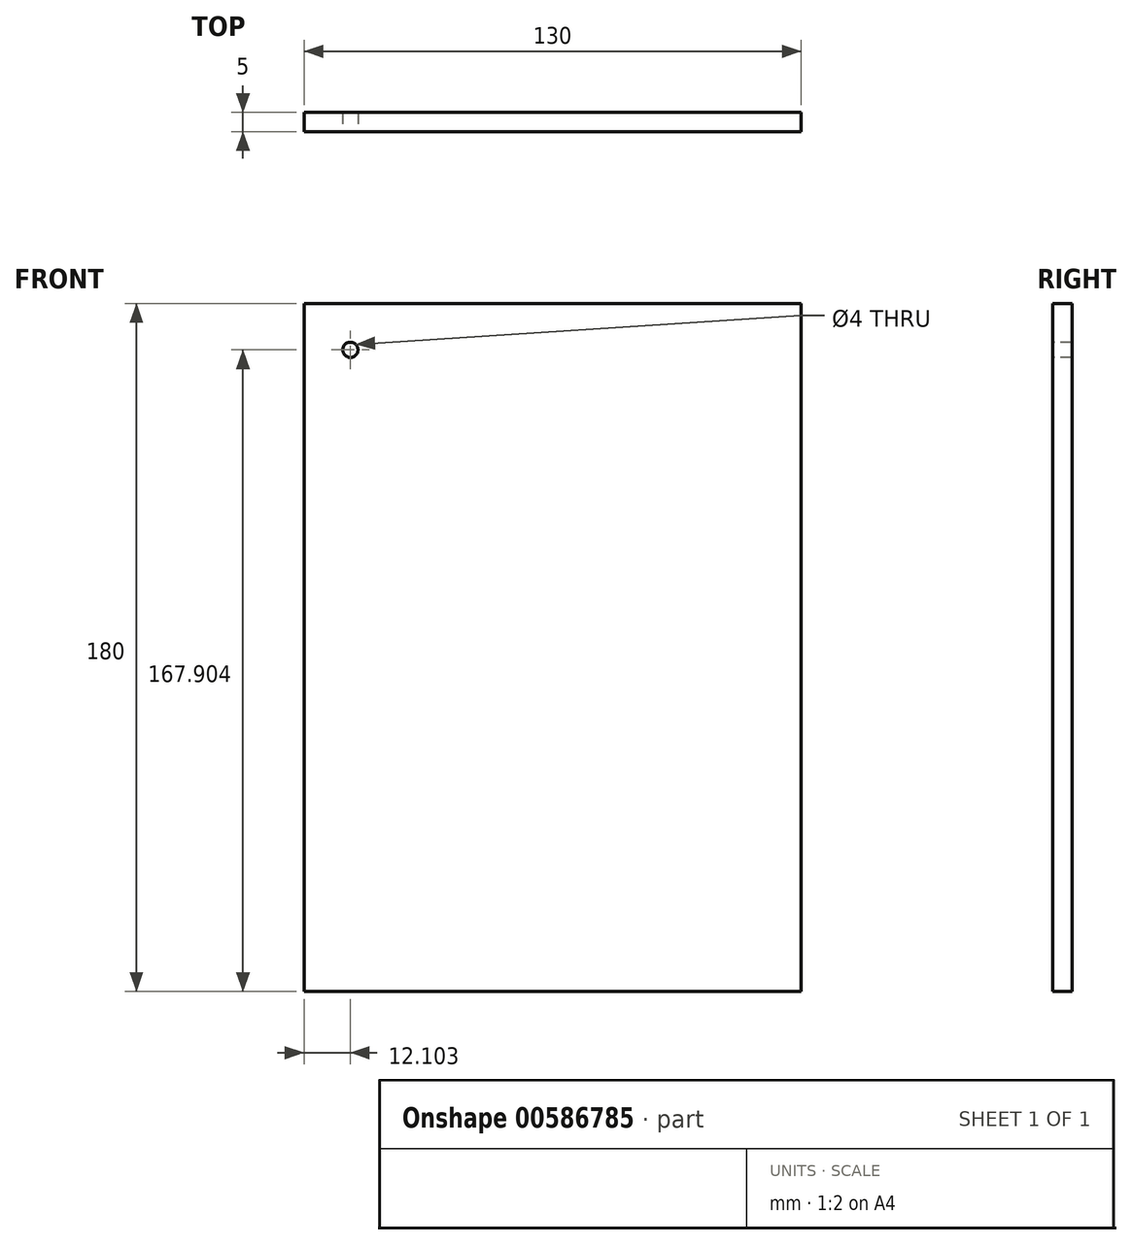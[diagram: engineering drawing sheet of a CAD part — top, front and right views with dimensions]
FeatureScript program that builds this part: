
annotation { "Feature Type Name" : "Feature", "Feature Type Description" : "" }
export const myFeature = defineFeature(function(context is Context, id is Id, definition is map)
    precondition{}
    {
        {
            var Q0;
            Q0=qCreatedBy(makeId("Front.planeOp"),FACE);
            var sketch = newSketch(context, id + "F0", { "sketchPlane" : qUnion([Q0])});
            skLineSegment(sketch, "E0.bottom", {"start": v(-69.83, 88.3) * mm, "end": v(60.17, 88.3) * mm});
            skLineSegment(sketch, "E0.top", {"start": v(-69.83, -91.7) * mm, "end": v(60.17, -91.7) * mm});
            skLineSegment(sketch, "E0.left", {"start": v(-69.83, 88.3) * mm, "end": v(-69.83, -91.7) * mm});
            skLineSegment(sketch, "E0.right", {"start": v(60.17, 88.3) * mm, "end": v(60.17, -91.7) * mm});
            skLineSegment(sketch, "E1", {"start": v(0, 88.3) * mm, "end": v(0, -91.7) * mm, "construction": true});
            skLineSegment(sketch, "E2", {"start": v(-69.83, -1.7) * mm, "end": v(60.17, -1.7) * mm, "construction": true});
            skSolve(sketch);
        }
        {
            var Q0;
            Q0 = qSketchRegion(id + "F0", true);
            extrude(context, id + "F1", {"entities" : qUnion([Q0]), "depth" : 5 * mm, "offsetDistance" : 25 * mm});
        }
        {
            var Q0;
            Q0=makeQuery(id+"F1.opExtrude","CAP_FACE",FACE,{"disambiguationData":[OSD([sQuery(id+"F0.wireOp",EDGE,"E0.bottom"),sQuery(id+"F0.wireOp",EDGE,"E0.top"),sQuery(id+"F0.wireOp",EDGE,"E0.left"),sQuery(id+"F0.wireOp",EDGE,"E0.right")])],"isStart":false});
            var sketch = newSketch(context, id + "F2", { "sketchPlane" : qUnion([Q0])});
            skCircle(sketch, "E3", {"center": v(-57.73, 76.2) * mm, "radius": 2.1 * mm});
            skLineSegment(sketch, "E4", {"start": v(0, 88.3) * mm, "end": v(0, -91.7) * mm, "construction": true});
            skLineSegment(sketch, "E5", {"start": v(-69.83, 0) * mm, "end": v(60.17, 0) * mm, "construction": true});
            skPoint(sketch, "E5.endSnap0", {"position": v(60.17, -1.7) * mm});
            skCircle(sketch, "E6.MirrorC", {"center": v(57.73, 76.2) * mm, "radius": 2.1 * mm});
            skSolve(sketch);
        }
        {
            var Q0;
            Q0=sQuery(id+"F2.wireOp",VERTEX,"E3.center");
            var Q1;
            Q1=makeQuery(id+"F1.opExtrude","SWEPT_BODY",BODY,{"disambiguationData":[OSD([sQuery(id+"F0.wireOp",EDGE,"E0.bottom"),sQuery(id+"F0.wireOp",EDGE,"E0.top"),sQuery(id+"F0.wireOp",EDGE,"E0.left"),sQuery(id+"F0.wireOp",EDGE,"E0.right")])]});
            hole(context, id + "F3", {"style" : HoleStyle.SIMPLE, "endStyle" : HoleEndStyle.THROUGH, "holeDiameter" : 4 * mm, "majorDiameter" : 5 * mm, "isTappedThrough" : true, "tappedDepth" : 12 * mm, "tapClearance" : 3, "locations" : qUnion([Q0]), "scope" : qUnion([Q1])});
        }
    });
